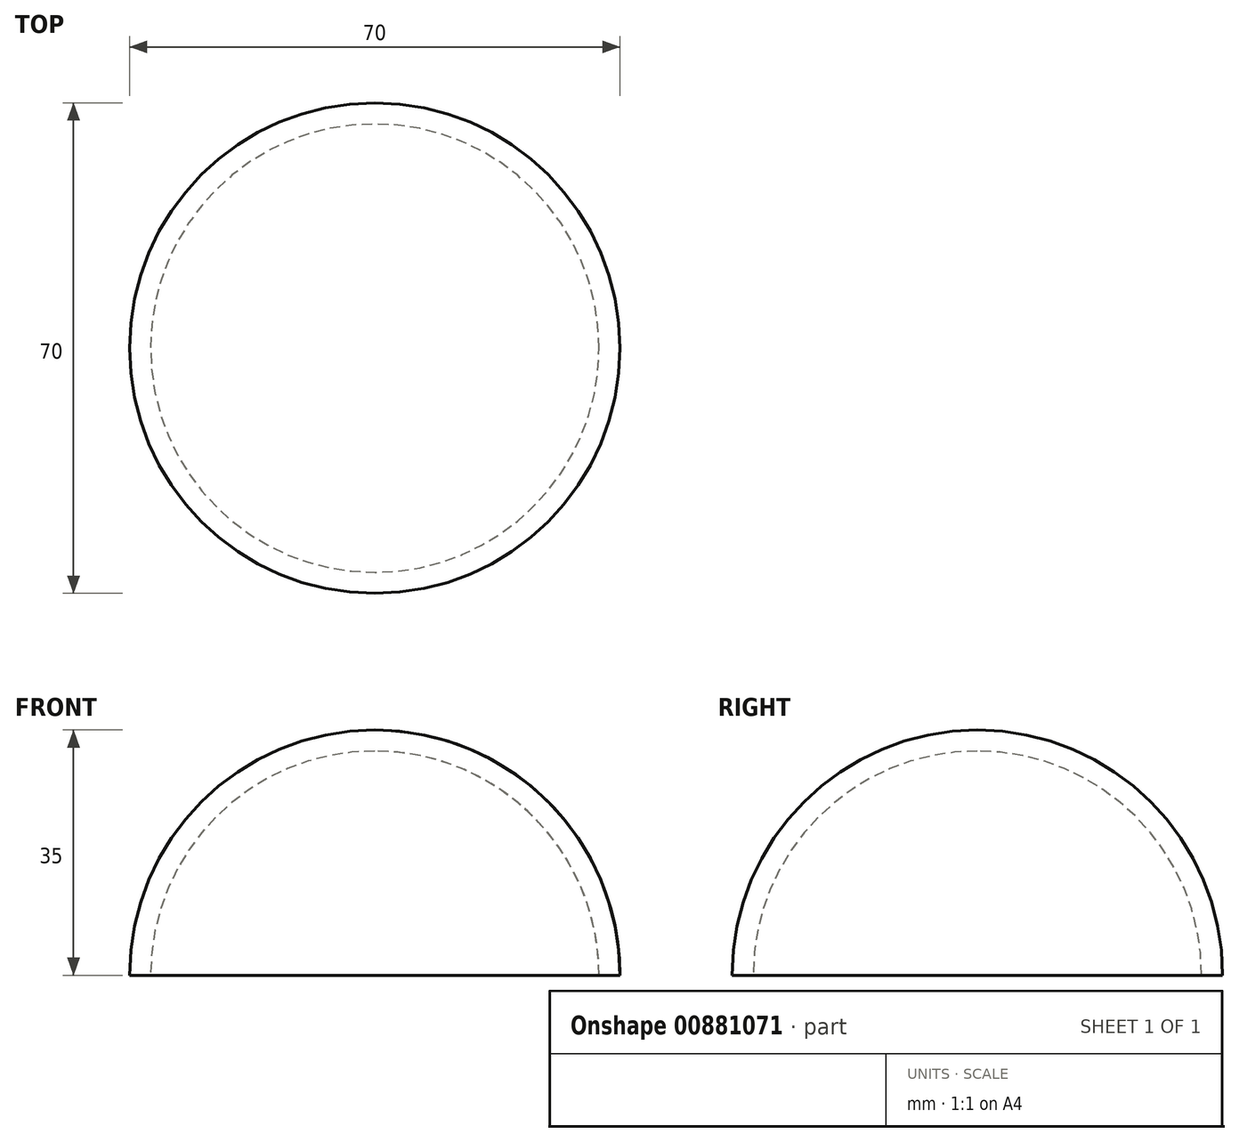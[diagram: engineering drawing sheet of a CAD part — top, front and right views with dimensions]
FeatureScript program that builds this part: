
annotation { "Feature Type Name" : "Feature", "Feature Type Description" : "" }
export const myFeature = defineFeature(function(context is Context, id is Id, definition is map)
    precondition{}
    {
        {
            var Q0;
            Q0=qCreatedBy(makeId("Front.planeOp"),FACE);
            var sketch = newSketch(context, id + "F0", { "sketchPlane" : qUnion([Q0])});
            skArc(sketch, "E0", {"start": v(35, 0) * mm, "mid": v(24.75, 24.75) * mm, "end": v(0, 35) * mm});
            skArc(sketch, "E1", {"start": v(32, 0) * mm, "mid": v(22.63, 22.63) * mm, "end": v(0, 32) * mm});
            skLineSegment(sketch, "E2", {"start": v(0, 35) * mm, "end": v(0, 32) * mm});
            skLineSegment(sketch, "E3", {"start": v(32, 0) * mm, "end": v(35, 0) * mm});
            skSolve(sketch);
        }
        {
            var Q0;
            Q0=makeQuery(id+"F0.imprint","IMPRINT",FACE,{"disambiguationData":[TD([[makeQuery(id+"F0.imprint","IMPRINT",EDGE,{"derivedFrom":sQuery(id+"F0.wireOp",EDGE,"E0")}),1.0]])]});
            var Q1;
            Q1=sQuery(id+"F0.wireOp",EDGE,"E2");
            revolve(context, id + "F1", {"surfaceOperationType" : NewSurfaceOperationType.NEW, "entities" : qUnion([Q0]), "axis" : qUnion([Q1]), "revolveType" : RevolveType.FULL});
        }
        {
            var Q0;
            Q0=qCreatedBy(makeId("Top.planeOp"),FACE);
            cPlane(context, id + "F2", {"entities" : qUnion([Q0]), "cplaneType" : CPlaneType.OFFSET, "offset" : 39.9 * mm, "width" : 150 * mm, "height" : 150 * mm});
        }
        {
            var Q0;
            Q0=qCreatedBy(id+"F2.planeOp",FACE);
            var sketch = newSketch(context, id + "F3", { "sketchPlane" : qUnion([Q0])});
            skFitSpline(sketch, "E4", {"points": [v(-12.08, 27.04) * mm, v(-23.76, 14.95) * mm, v(-27.65, -6.35) * mm, v(-20.9, -20.48) * mm, v(-10.24, -27.65) * mm, v(-4.5, -23.55) * mm, v(-7.17, 27.24) * mm, v(-12.08, 27.04) * mm]});
            skFitSpline(sketch, "E5.MirrorC", {"points": [v(12.08, 27.04) * mm, v(23.76, 14.95) * mm, v(27.65, -6.35) * mm, v(20.9, -20.48) * mm, v(10.24, -27.65) * mm, v(4.5, -23.55) * mm, v(7.17, 27.24) * mm, v(12.08, 27.04) * mm]});
            skSolve(sketch);
        }
        {
            var Q0;
            Q0=makeQuery(id+"F3.imprint","IMPRINT",FACE,{"disambiguationData":[TD([[makeQuery(id+"F3.imprint","IMPRINT",EDGE,{"derivedFrom":sQuery(id+"F3.wireOp",EDGE,"E4")}),1.0]])]});
            var Q1;
            Q1=makeQuery(id+"F3.imprint","IMPRINT",FACE,{"disambiguationData":[TD([[makeQuery(id+"F3.imprint","IMPRINT",EDGE,{"derivedFrom":sQuery(id+"F3.wireOp",EDGE,"E5.MirrorC")}),-1.0]])]});
            var Q2;
            Q2=sQuery(id+"F3.wireOp",EDGE,"E4");
            var Q3;
            Q3=sQuery(id+"F3.wireOp",EDGE,"E5.MirrorC");
            extrude(context, id + "F4", {"entities" : qUnion([Q0, Q1]), "bodyType" : ToolBodyType.SURFACE, "surfaceEntities" : qUnion([Q2, Q3]), "oppositeDirection" : true, "depth" : 25 * mm, "offsetDistance" : 25 * mm});
        }
    });
